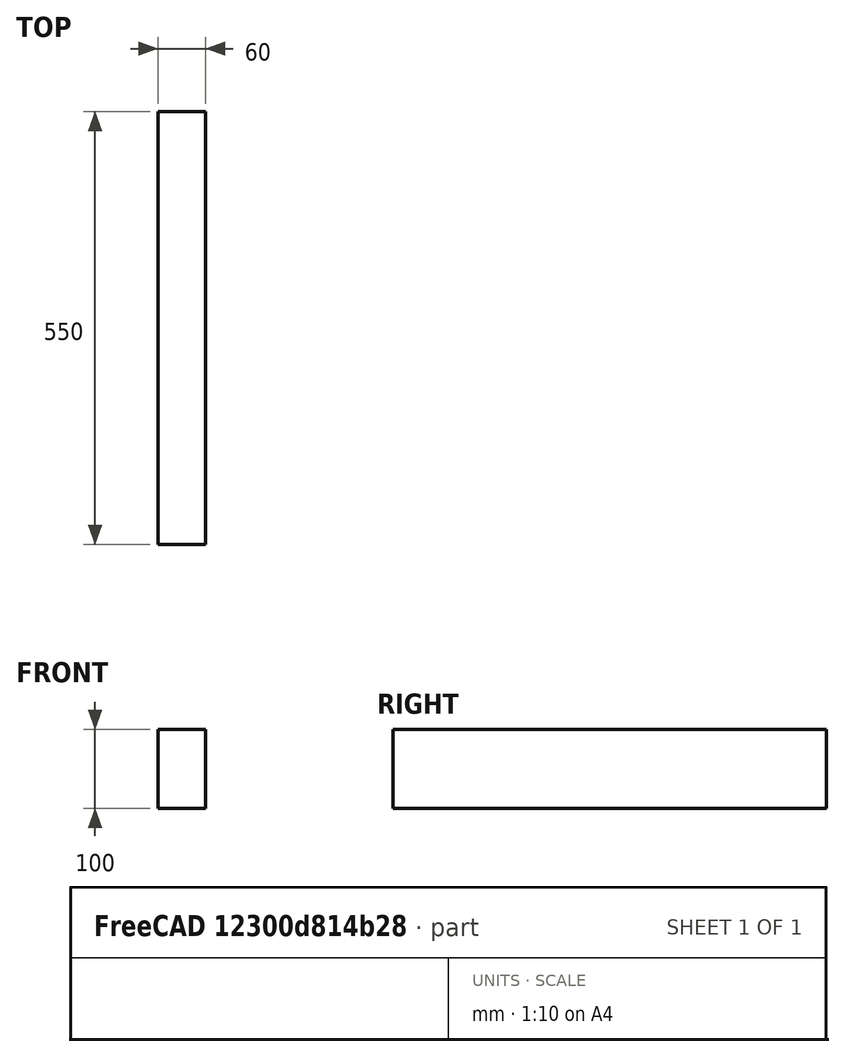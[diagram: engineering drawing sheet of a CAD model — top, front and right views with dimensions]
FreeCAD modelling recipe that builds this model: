
FCSTD DOCUMENT  (FreeCAD 1.0RUnknown)
Label: beam60x100x400
License: All rights reserved
LicenseURL: https://en.wikipedia.org/wiki/All_rights_reserved
objects: PartDesign::CoordinateSystem×3, Sketcher::SketchObject×1, PartDesign::Pad×1, PartDesign::Body×1, App::Part×1
note: 9 computed .brp shape members not serialized (recipe doc carries the construction recipe); baked Part::Feature solids carry a one-line shape summary decoded from their .brp

FEATURE [Sketcher::SketchObject] Sketch
  ArcFitTolerance = 1e-06
  AttachmentSupport = -> [XZ_Plane]
  FullyConstrained = true
  MakeInternals = false
  MapMode = 5
  Placement = pos=(0,0,0) rot=(1,0,0;1.5708rad)
  sketch-geometry (5):
    g0: LineSegment StartX=-30 StartY=-50 StartZ=0 EndX=30 EndY=-50 EndZ=0
    g1: LineSegment StartX=30 StartY=-50 StartZ=0 EndX=30 EndY=50 EndZ=0
    g2: LineSegment StartX=30 StartY=50 StartZ=0 EndX=-30 EndY=50 EndZ=0
    g3: LineSegment StartX=-30 StartY=50 StartZ=0 EndX=-30 EndY=-50 EndZ=0
    g4: GeomPoint [constr] X=0 Y=0 Z=0
  constraints (12):
    c: Coincident(g0,g1)
    c: Coincident(g1,g2)
    c: Coincident(g2,g3)
    c: Coincident(g3,g0)
    c: Horizontal(g0)
    c: Horizontal(g2)
    c: Vertical(g1)
    c: Vertical(g3)
    c: Symmetric(g2,g0,g4)
    c: Coincident(g4,g-1)
    c: DistanceX(g0,g0) = 60
    c: DistanceY(g3,g3) = 100
FEATURE [PartDesign::Pad] Pad
  Direction = (0,-1,2e-16)
  Length = 550
  Length2 = 10
  Midplane = true
  Placement = pos=(0,0,0) rot=(1,0,0;1.5708rad)
  Profile = -> Sketch
  ReferenceAxis = -> Sketch [N_Axis]
  Refine = true
  Suppressed = false
  Type = 0
FEATURE [PartDesign::Body] Body  label="Körper"
  AllowCompound = false
  Group = -> [Sketch,Pad]
  Origin = -> Origin
  Tip = -> Pad
FEATURE [PartDesign::CoordinateSystem] LCS_Origin
  AttacherType = Attacher::AttachEngine3D
  AttachmentSupport = -> [X_Axis001]
  MapMode = 2
FEATURE [PartDesign::CoordinateSystem] LCS_1
  AttacherType = Attacher::AttachEngine3D
  AttachmentSupport = -> [Pad]
  MapMode = 45
  Placement = pos=(-30,275,-6.11e-14) rot=(0,0,1;0rad)
FEATURE [PartDesign::CoordinateSystem] LCS_2
  AttacherType = Attacher::AttachEngine3D
  AttachmentSupport = -> [Pad]
  MapMode = 45
  Placement = pos=(-30,-275,6.11e-14) rot=(0,0,1;0rad)
FEATURE [App::Part] beam60x100x887  label="beam60x100x400"
  Group = -> [LCS_Origin,Body,LCS_1,LCS_2]
  Origin = -> Origin001
